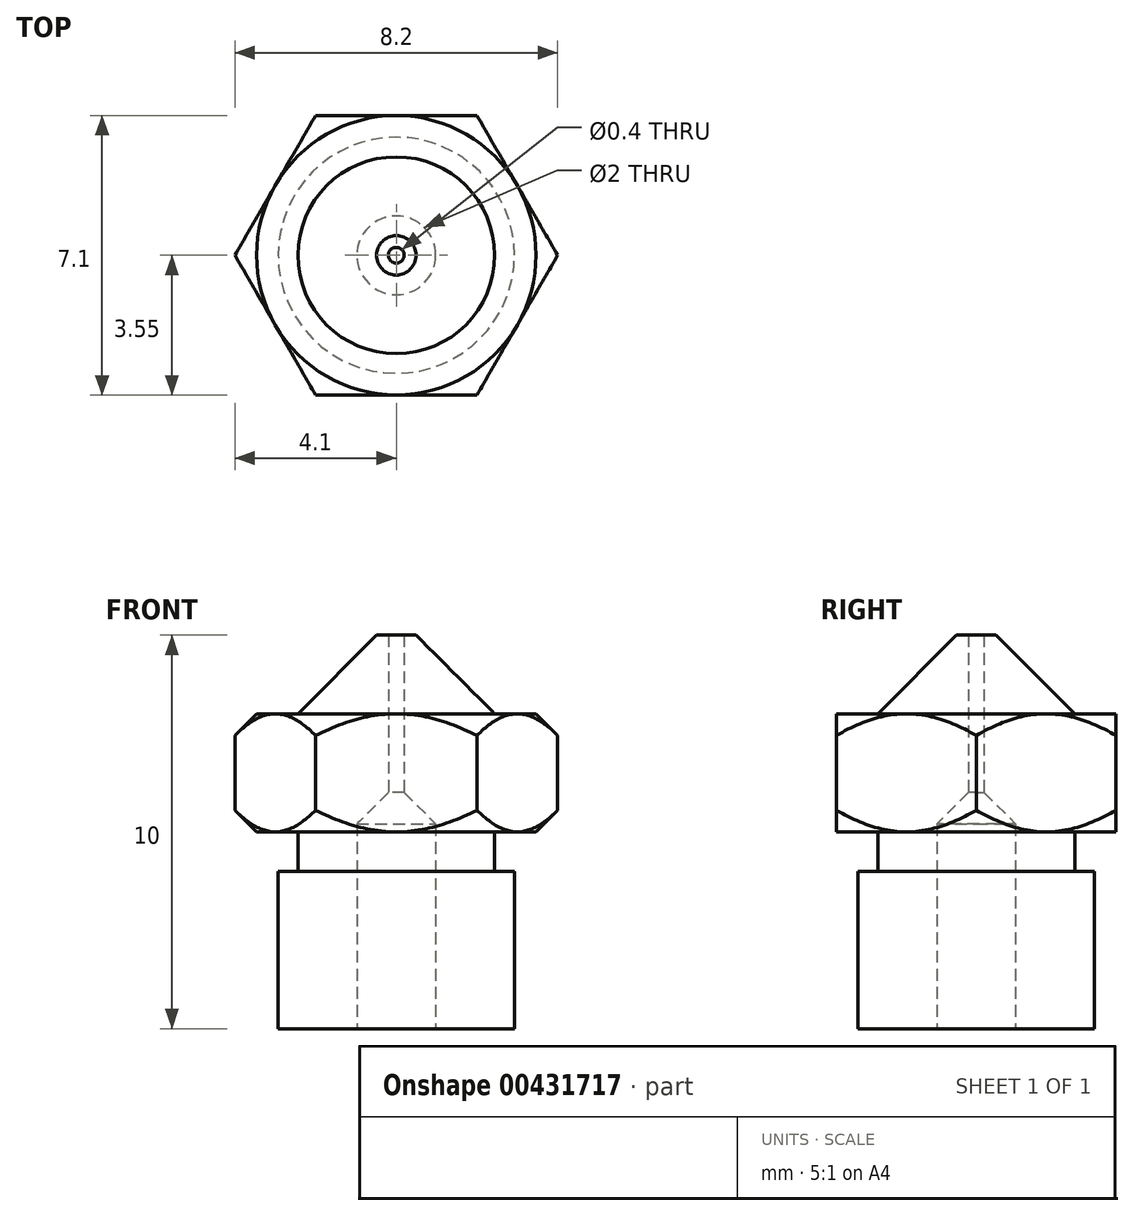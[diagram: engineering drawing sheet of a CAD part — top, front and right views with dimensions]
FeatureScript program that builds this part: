
annotation { "Feature Type Name" : "Feature", "Feature Type Description" : "" }
export const myFeature = defineFeature(function(context is Context, id is Id, definition is map)
    precondition{}
    {
        {
            var Q0;
            Q0=qCreatedBy(makeId("Top.planeOp"),FACE);
            var sketch = newSketch(context, id + "F0", { "sketchPlane" : qUnion([Q0])});
            skCircle(sketch, "E0.cCircle", {"center": v(0, 0) * mm, "radius": 3.55 * mm, "construction": true});
            skLineSegment(sketch, "E0.0", {"start": v(-2.05, 3.55) * mm, "end": v(2.05, 3.55) * mm});
            skLineSegment(sketch, "E0.1", {"start": v(2.05, 3.55) * mm, "end": v(4.1, 0) * mm});
            skLineSegment(sketch, "E0.2", {"start": v(4.1, 0) * mm, "end": v(2.05, -3.55) * mm});
            skLineSegment(sketch, "E0.3", {"start": v(2.05, -3.55) * mm, "end": v(-2.05, -3.55) * mm});
            skLineSegment(sketch, "E0.4", {"start": v(-2.05, -3.55) * mm, "end": v(-4.1, 0) * mm});
            skLineSegment(sketch, "E0.5", {"start": v(-4.1, 0) * mm, "end": v(-2.05, 3.55) * mm});
            skPoint(sketch, "E0.0.midPoint", {"position": v(0, 3.55) * mm});
            skCircle(sketch, "E1", {"center": v(0, 0) * mm, "radius": 4.1 * mm});
            skCircle(sketch, "E2", {"center": v(0, 0) * mm, "radius": 2.5 * mm});
            skCircle(sketch, "E3", {"center": v(0, 0) * mm, "radius": 0.2 * mm});
            skSolve(sketch);
        }
        {
            var Q0;
            Q0=makeQuery(id+"F0.imprint","IMPRINT",FACE,{"disambiguationData":[TD([[makeQuery(id+"F0.imprint","IMPRINT",EDGE,{"derivedFrom":sQuery(id+"F0.wireOp",EDGE,"E0.0")}),-1.0]])]});
            var Q1;
            {var subQ0=sQuery(id+"F0.wireOp",EDGE,"E0.5");Q1=makeQuery(id+"F0.imprint","IMPRINT",FACE,{"disambiguationData":[TD([[makeQuery(id+"F0.imprint","IMPRINT",EDGE,{"derivedFrom":subQ0}),1.0]])]});}
            var Q2;
            {var subQ0=sQuery(id+"F0.wireOp",EDGE,"E0.4");Q2=makeQuery(id+"F0.imprint","IMPRINT",FACE,{"disambiguationData":[TD([[makeQuery(id+"F0.imprint","IMPRINT",EDGE,{"derivedFrom":subQ0}),1.0]])]});}
            var Q3;
            {var subQ0=sQuery(id+"F0.wireOp",EDGE,"E0.0");Q3=makeQuery(id+"F0.imprint","IMPRINT",FACE,{"disambiguationData":[TD([[makeQuery(id+"F0.imprint","IMPRINT",EDGE,{"derivedFrom":subQ0}),1.0]])]});}
            var Q4;
            {var subQ0=sQuery(id+"F0.wireOp",EDGE,"E0.1");Q4=makeQuery(id+"F0.imprint","IMPRINT",FACE,{"disambiguationData":[TD([[makeQuery(id+"F0.imprint","IMPRINT",EDGE,{"derivedFrom":subQ0}),1.0]])]});}
            var Q5;
            {var subQ0=sQuery(id+"F0.wireOp",EDGE,"E0.2");Q5=makeQuery(id+"F0.imprint","IMPRINT",FACE,{"disambiguationData":[TD([[makeQuery(id+"F0.imprint","IMPRINT",EDGE,{"derivedFrom":subQ0}),1.0]])]});}
            var Q6;
            {var subQ0=sQuery(id+"F0.wireOp",EDGE,"E0.3");Q6=makeQuery(id+"F0.imprint","IMPRINT",FACE,{"disambiguationData":[TD([[makeQuery(id+"F0.imprint","IMPRINT",EDGE,{"derivedFrom":subQ0}),1.0]])]});}
            var Q7;
            Q7=makeQuery(id+"F0.imprint","IMPRINT",FACE,{"disambiguationData":[TD([[makeQuery(id+"F0.imprint","IMPRINT",EDGE,{"derivedFrom":sQuery(id+"F0.wireOp",EDGE,"E2")}),1.0]])]});
            var Q8;
            Q8=sQuery(id+"F0.wireOp",EDGE,"E1");
            extrude(context, id + "F1", {"entities" : qUnion([Q0, Q1, Q2, Q3, Q4, Q5, Q6, Q7]), "flatOperationType" : FlatOperationType.REMOVE, "surfaceEntities" : qUnion([Q8]), "offsetDistance" : 25 * mm, "depth" : 3 * mm, "domain" : OperationDomain.MODEL});
        }
        {
            var Q0;
            Q0=makeQuery(id+"F1.opExtrude","CAP_EDGE",EDGE,{"disambiguationData":[OSD([sQuery(id+"F0.wireOp",EDGE,"E1")])],"isStart":false});
            var Q1;
            Q1=makeQuery(id+"F1.opExtrude","CAP_EDGE",EDGE,{"disambiguationData":[OSD([sQuery(id+"F0.wireOp",EDGE,"E1")])],"isStart":true});
            chamfer(context, id + "F2", {"entities" : qUnion([Q0, Q1]), "width" : 0.55 * mm, "tangentPropagation" : true});
        }
        {
            var Q0;
            {var subQ0=sQuery(id+"F0.wireOp",EDGE,"E0.3");Q0=makeQuery(id+"F0.imprint","IMPRINT",FACE,{"disambiguationData":[TD([[makeQuery(id+"F0.imprint","IMPRINT",EDGE,{"derivedFrom":subQ0}),1.0]])]});}
            var Q1;
            {var subQ0=sQuery(id+"F0.wireOp",EDGE,"E0.2");Q1=makeQuery(id+"F0.imprint","IMPRINT",FACE,{"disambiguationData":[TD([[makeQuery(id+"F0.imprint","IMPRINT",EDGE,{"derivedFrom":subQ0}),1.0]])]});}
            var Q2;
            {var subQ0=sQuery(id+"F0.wireOp",EDGE,"E0.4");Q2=makeQuery(id+"F0.imprint","IMPRINT",FACE,{"disambiguationData":[TD([[makeQuery(id+"F0.imprint","IMPRINT",EDGE,{"derivedFrom":subQ0}),1.0]])]});}
            var Q3;
            {var subQ0=sQuery(id+"F0.wireOp",EDGE,"E0.1");Q3=makeQuery(id+"F0.imprint","IMPRINT",FACE,{"disambiguationData":[TD([[makeQuery(id+"F0.imprint","IMPRINT",EDGE,{"derivedFrom":subQ0}),1.0]])]});}
            var Q4;
            {var subQ0=sQuery(id+"F0.wireOp",EDGE,"E0.0");Q4=makeQuery(id+"F0.imprint","IMPRINT",FACE,{"disambiguationData":[TD([[makeQuery(id+"F0.imprint","IMPRINT",EDGE,{"derivedFrom":subQ0}),1.0]])]});}
            var Q5;
            {var subQ0=sQuery(id+"F0.wireOp",EDGE,"E0.5");Q5=makeQuery(id+"F0.imprint","IMPRINT",FACE,{"disambiguationData":[TD([[makeQuery(id+"F0.imprint","IMPRINT",EDGE,{"derivedFrom":subQ0}),1.0]])]});}
            extrude(context, id + "F3", {"entities" : qUnion([Q0, Q1, Q2, Q3, Q4, Q5]), "operationType" : NewBodyOperationType.REMOVE, "flatOperationType" : FlatOperationType.REMOVE, "endBound" : BoundingType.THROUGH_ALL, "offsetDistance" : 25 * mm, "depth" : 25 * mm, "domain" : OperationDomain.MODEL});
        }
        {
            var Q0;
            Q0=makeQuery(id+"F0.imprint","IMPRINT",FACE,{"disambiguationData":[TD([[makeQuery(id+"F0.imprint","IMPRINT",EDGE,{"derivedFrom":sQuery(id+"F0.wireOp",EDGE,"E2")}),1.0]])]});
            extrude(context, id + "F4", {"entities" : qUnion([Q0]), "operationType" : NewBodyOperationType.ADD, "flatOperationType" : FlatOperationType.REMOVE, "offsetDistance" : 25 * mm, "depth" : 5 * mm, "domain" : OperationDomain.MODEL});
        }
        {
            var Q0;
            Q0=makeQuery(id+"F4.opExtrude","CAP_EDGE",EDGE,{"disambiguationData":[OSD([sQuery(id+"F0.wireOp",EDGE,"E2")])],"isStart":false});
            chamfer(context, id + "F5", {"entities" : qUnion([Q0]), "width" : 2 * mm, "tangentPropagation" : true});
        }
        {
            var Q0;
            Q0=makeQuery(id+"F0.imprint","IMPRINT",FACE,{"disambiguationData":[TD([[makeQuery(id+"F0.imprint","IMPRINT",EDGE,{"derivedFrom":sQuery(id+"F0.wireOp",EDGE,"E2")}),1.0]])]});
            extrude(context, id + "F6", {"entities" : qUnion([Q0]), "operationType" : NewBodyOperationType.ADD, "flatOperationType" : FlatOperationType.REMOVE, "oppositeDirection" : true, "offsetDistance" : 25 * mm, "depth" : 1 * mm, "domain" : OperationDomain.MODEL});
        }
        {
            var Q0;
            Q0=makeQuery(id+"F6.opExtrude","CAP_FACE",FACE,{"disambiguationData":[OSD([sQuery(id+"F0.wireOp",EDGE,"E2"),sQuery(id+"F0.wireOp",EDGE,"E3")])],"isStart":false});
            var sketch = newSketch(context, id + "F7", { "sketchPlane" : qUnion([Q0])});
            skCircle(sketch, "E4", {"center": v(0, 0) * mm, "radius": 3 * mm});
            skSolve(sketch);
        }
        {
            var Q0;
            Q0=makeQuery(id+"F7.imprint","IMPRINT",FACE,{"disambiguationData":[TD([[makeQuery(id+"F7.imprint","IMPRINT",EDGE,{"derivedFrom":makeQuery(id+"F6.opExtrude","CAP_EDGE",EDGE,{"disambiguationData":[OSD([sQuery(id+"F0.wireOp",EDGE,"E2")])],"isStart":false})}),-1.0]])]});
            var Q1;
            Q1=makeQuery(id+"F7.imprint","IMPRINT",FACE,{"disambiguationData":[TD([[makeQuery(id+"F7.imprint","IMPRINT",EDGE,{"derivedFrom":sQuery(id+"F7.wireOp",EDGE,"E4")}),1.0]])]});
            extrude(context, id + "F8", {"entities" : qUnion([Q0, Q1]), "operationType" : NewBodyOperationType.ADD, "depth" : 4 * mm});
        }
        {
            var Q0;
            Q0=makeQuery(id+"F8.opExtrude","CAP_FACE",FACE,{"disambiguationData":[OSD([sQuery(id+"F0.wireOp",EDGE,"E3"),sQuery(id+"F7.wireOp",EDGE,"E4")])],"isStart":false});
            var sketch = newSketch(context, id + "F9", { "sketchPlane" : qUnion([Q0])});
            skCircle(sketch, "E5", {"center": v(0, 0) * mm, "radius": 1 * mm});
            skSolve(sketch);
        }
        {
            var Q0;
            Q0=makeQuery(id+"F9.imprint","IMPRINT",FACE,{"disambiguationData":[TD([[makeQuery(id+"F9.imprint","IMPRINT",EDGE,{"derivedFrom":sQuery(id+"F9.wireOp",EDGE,"E5")}),1.0]])]});
            extrude(context, id + "F10", {"entities" : qUnion([Q0]), "operationType" : NewBodyOperationType.REMOVE, "oppositeDirection" : true, "depth" : 6 * mm});
        }
        {
            var Q0;
            Q0=makeQuery(id+"F10.boolean.opBoolean","COPY",EDGE,{"derivedFrom":makeQuery(id+"F10.opExtrude","CAP_EDGE",EDGE,{"disambiguationData":[OSD([sQuery(id+"F9.wireOp",EDGE,"E5")])],"isStart":false})});
            chamfer(context, id + "F11", {"entities" : qUnion([Q0]), "width" : 0.8 * mm, "tangentPropagation" : true});
        }
    });
